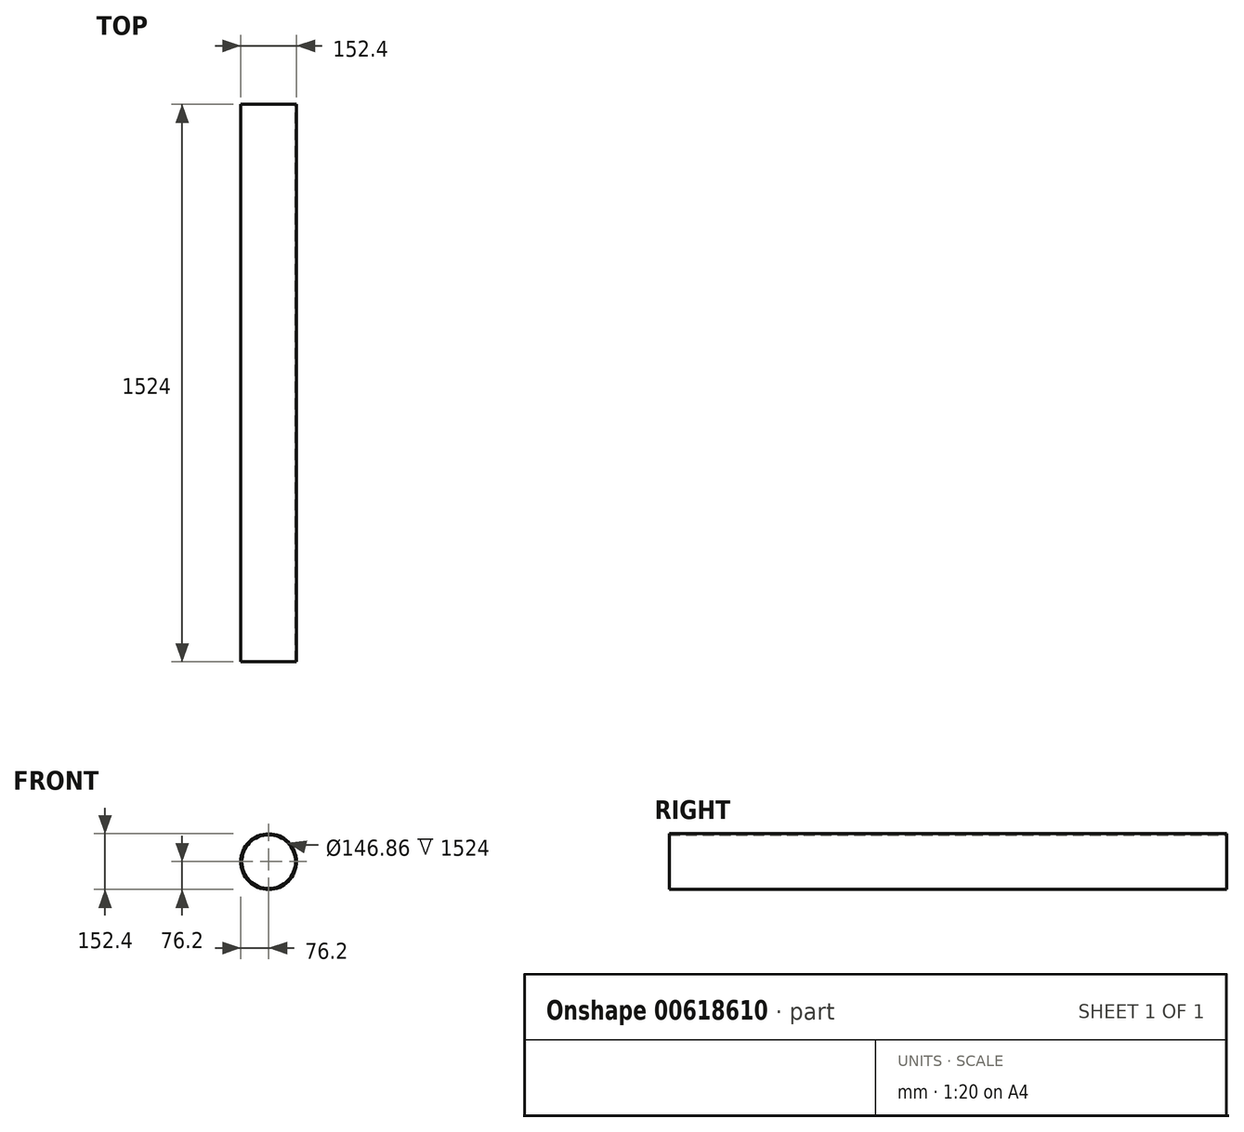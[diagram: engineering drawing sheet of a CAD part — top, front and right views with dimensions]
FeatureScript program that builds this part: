
annotation { "Feature Type Name" : "Feature", "Feature Type Description" : "" }
export const myFeature = defineFeature(function(context is Context, id is Id, definition is map)
    precondition{}
    {
        {
            var Q0;
            Q0=qCreatedBy(makeId("Front.planeOp"),FACE);
            var sketch = newSketch(context, id + "F0", { "sketchPlane" : qUnion([Q0])});
            skCircle(sketch, "E0", {"center": v(0, 0) * mm, "radius": 76.2 * mm});
            skCircle(sketch, "E1", {"center": v(0, 0) * mm, "radius": 73.43 * mm});
            skSolve(sketch);
        }
        {
            var Q0;
            Q0=makeQuery(id+"F0.imprint","IMPRINT",FACE,{"disambiguationData":[TD([[makeQuery(id+"F0.imprint","IMPRINT",EDGE,{"derivedFrom":sQuery(id+"F0.wireOp",EDGE,"E0")}),1.0]])]});
            extrude(context, id + "F1", {"entities" : qUnion([Q0]), "depth" : 1524 * mm, "offsetDistance" : 25.4 * mm});
        }
    });
